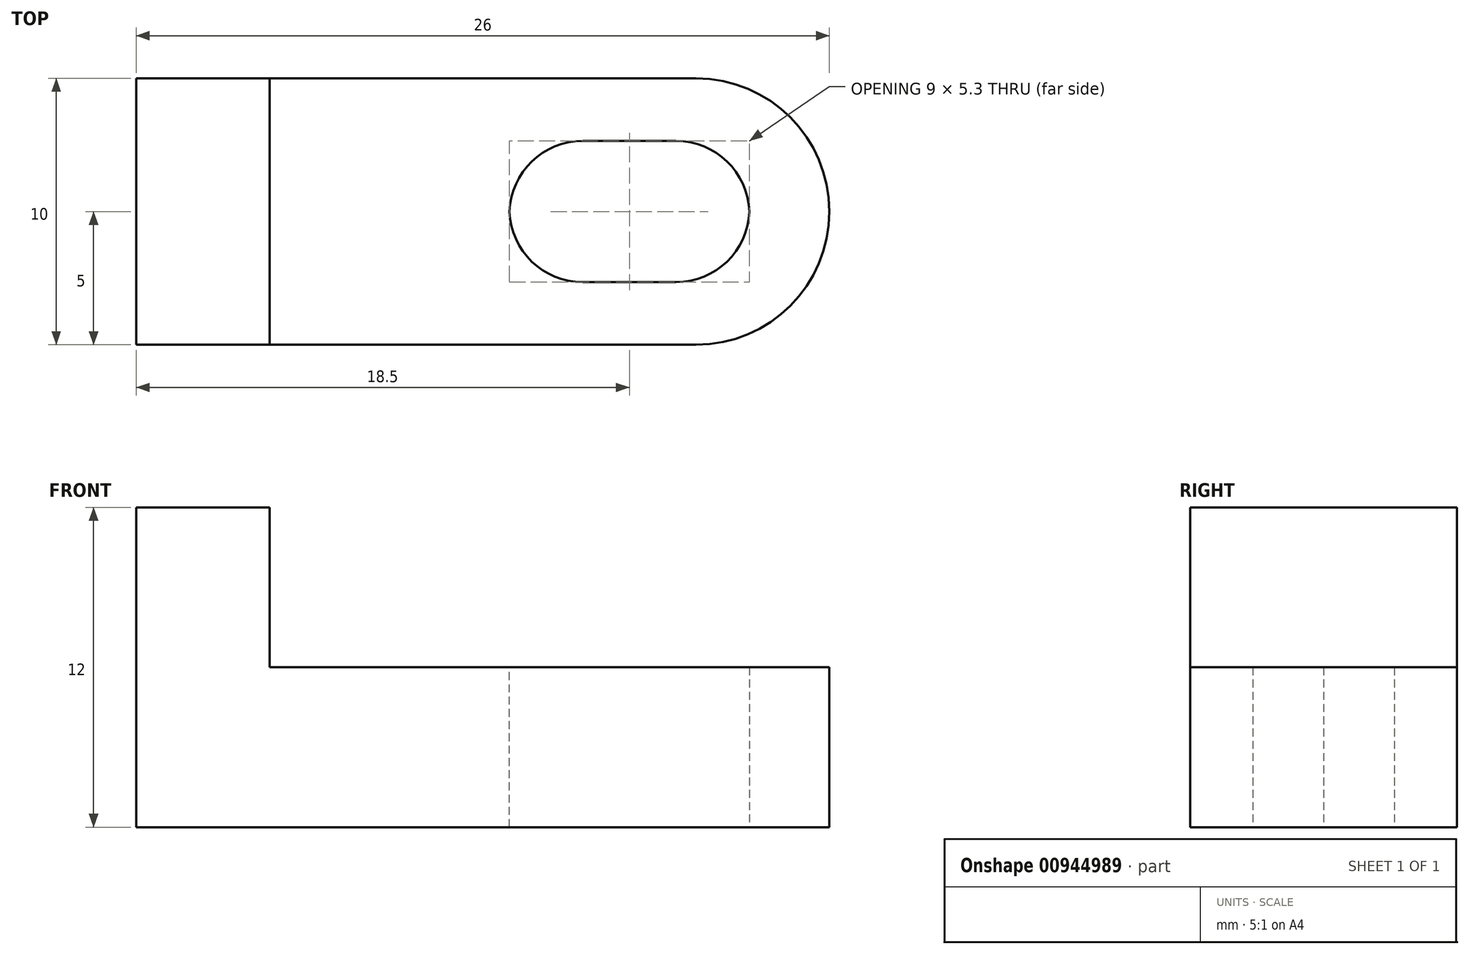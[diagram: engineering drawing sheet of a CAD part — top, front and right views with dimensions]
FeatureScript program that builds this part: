
annotation { "Feature Type Name" : "Feature", "Feature Type Description" : "" }
export const myFeature = defineFeature(function(context is Context, id is Id, definition is map)
    precondition{}
    {
        {
            var Q0;
            Q0=qCreatedBy(makeId("Top.planeOp"),FACE);
            var sketch = newSketch(context, id + "F0", { "sketchPlane" : qUnion([Q0])});
            skLineSegment(sketch, "E0.bottom", {"start": v(0, 0) * mm, "end": v(-26, 0) * mm});
            skLineSegment(sketch, "E0.top", {"start": v(0, 10) * mm, "end": v(-26, 10) * mm});
            skLineSegment(sketch, "E0.left", {"start": v(0, 0) * mm, "end": v(0, 10) * mm});
            skLineSegment(sketch, "E0.right", {"start": v(-26, 0) * mm, "end": v(-26, 10) * mm});
            skLineSegment(sketch, "E1.bottom", {"start": v(-12, 2.35) * mm, "end": v(-3, 2.35) * mm});
            skLineSegment(sketch, "E1.top", {"start": v(-12, 7.65) * mm, "end": v(-3, 7.65) * mm});
            skLineSegment(sketch, "E1.left", {"start": v(-12, 2.35) * mm, "end": v(-12, 7.65) * mm});
            skLineSegment(sketch, "E1.right", {"start": v(-3, 2.35) * mm, "end": v(-3, 7.65) * mm});
            skPoint(sketch, "E1.middle", {"position": v(-7.5, 5) * mm});
            skPoint(sketch, "E1.middle.positionSnap0", {"position": v(0, 5) * mm});
            skPoint(sketch, "E1.centerSnap0", {"position": v(0, 5) * mm});
            skLineSegment(sketch, "E2", {"start": v(-21, 10) * mm, "end": v(-21, 0) * mm});
            skLineSegment(sketch, "E3", {"start": v(-11, 10) * mm, "end": v(-11, 0) * mm, "construction": true});
            skSolve(sketch);
        }
        {
            var Q0;
            Q0 = qSketchRegion(id + "F0", true);
            extrude(context, id + "F1", {"entities" : qUnion([Q0]), "depth" : 6 * mm, "offsetDistance" : 25 * mm});
        }
        {
            var Q0;
            {var subQ0=sQuery(id+"F0.wireOp",EDGE,"E0.right");Q0=makeQuery(id+"F0.imprint","IMPRINT",FACE,{"disambiguationData":[TD([[makeQuery(id+"F0.imprint","IMPRINT",EDGE,{"derivedFrom":subQ0}),-1.0]])]});}
            extrude(context, id + "F2", {"entities" : qUnion([Q0]), "operationType" : NewBodyOperationType.ADD, "depth" : 12 * mm, "offsetDistance" : 25 * mm});
        }
        {
            var Q0;
            Q0=makeQuery(id+"F1.opExtrude","SWEPT_EDGE",EDGE,{"disambiguationData":[OSD([sQuery(id+"F0.wireOp",EDGE,"E1.top"),sQuery(id+"F0.wireOp",EDGE,"E1.left")])]});
            var Q1;
            Q1=makeQuery(id+"F1.opExtrude","SWEPT_EDGE",EDGE,{"disambiguationData":[OSD([sQuery(id+"F0.wireOp",EDGE,"E1.bottom"),sQuery(id+"F0.wireOp",EDGE,"E1.left")])]});
            var Q2;
            Q2=makeQuery(id+"F1.opExtrude","SWEPT_EDGE",EDGE,{"disambiguationData":[OSD([sQuery(id+"F0.wireOp",EDGE,"E1.top"),sQuery(id+"F0.wireOp",EDGE,"E1.right")])]});
            var Q3;
            Q3=makeQuery(id+"F1.opExtrude","SWEPT_EDGE",EDGE,{"disambiguationData":[OSD([sQuery(id+"F0.wireOp",EDGE,"E1.bottom"),sQuery(id+"F0.wireOp",EDGE,"E1.right")])]});
            fillet(context, id + "F3", {"entities" : qUnion([Q0, Q1, Q2, Q3]), "radius" : 2.75 * mm, "tangentPropagation" : true, "allowEdgeOverflow" : false});
        }
        {
            var Q0;
            Q0=makeQuery(id+"F1.opExtrude","SWEPT_EDGE",EDGE,{"disambiguationData":[OSD([sQuery(id+"F0.wireOp",EDGE,"E0.bottom"),sQuery(id+"F0.wireOp",EDGE,"E0.left")])]});
            var Q1;
            Q1=makeQuery(id+"F1.opExtrude","SWEPT_EDGE",EDGE,{"disambiguationData":[OSD([sQuery(id+"F0.wireOp",EDGE,"E0.top"),sQuery(id+"F0.wireOp",EDGE,"E0.left")])]});
            fillet(context, id + "F4", {"entities" : qUnion([Q0, Q1]), "radius" : 5 * mm, "tangentPropagation" : true, "allowEdgeOverflow" : false});
        }
    });
